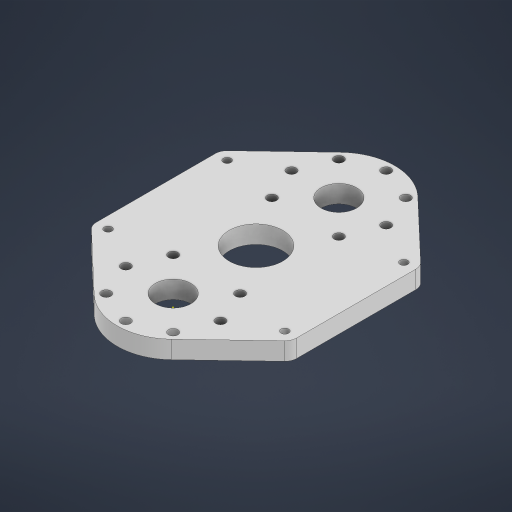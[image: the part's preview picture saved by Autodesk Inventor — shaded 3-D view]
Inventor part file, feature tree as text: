
AUTODESK INVENTOR PART (.ipt)
format: ipt  version: 2024.3 (Build 283343000, 343)  size: 246,784 bytes
history: native  units: in
note: dims shown in document units (in); Inventor stores cm internally (conversion verified against a paired STEP export)
features: sketch x2, extrude x1
ambient origin geometry x8: Origin, YZ Plane, XZ Plane, XY Plane, X Axis, Y Axis, Z Axis, Center Point
bodies: Solid1 (feature_tree)
feature tree (3):
  sketch  "Sketch1"  dims[d0=0.5in d1=3.0in]
  extrude  "Extrusion1"  Depth=3.0in
  sketch  "Sketch2"  dims[d2=2.0in d3=0.196in d4=3.1496in d6=360.0deg d8=0.196in d9=3.1496in d11=360.0deg d13=0.75in d14=0.75in d15=2.36in d16=2.36in d17=0.5in d18=0.159in d24=0.5in d25=1.13in d26=0.25in d27=0.125in d28=0.0in d29=0.0in]
